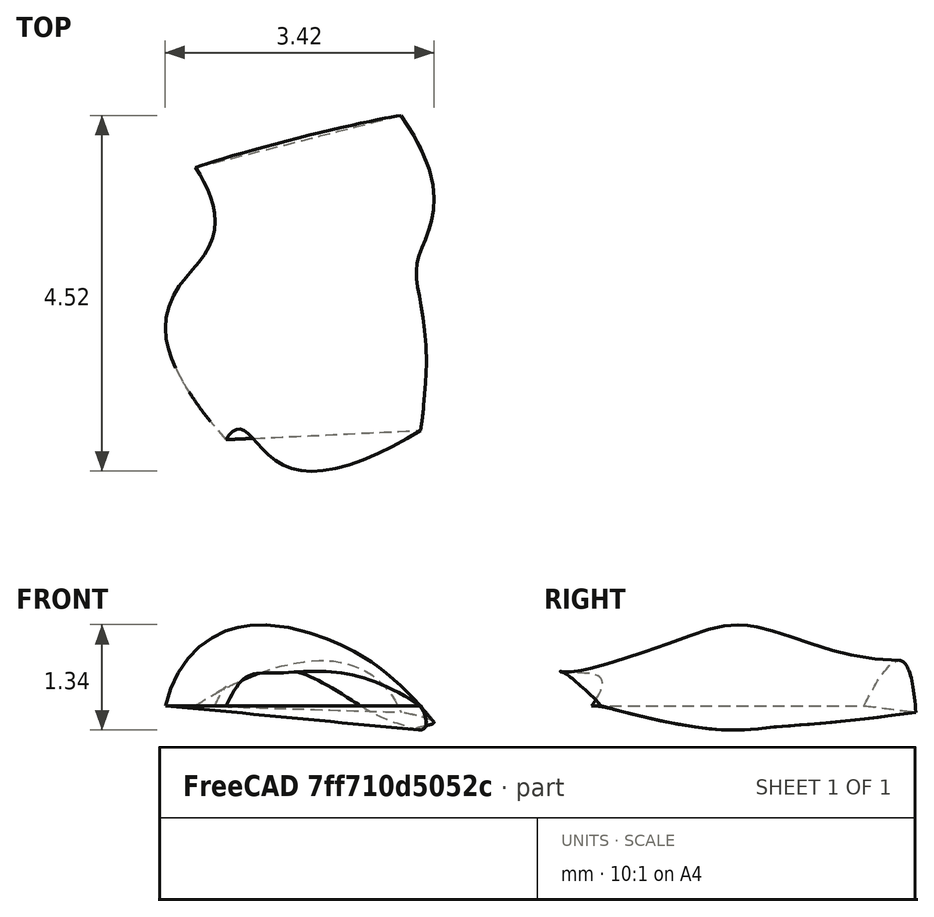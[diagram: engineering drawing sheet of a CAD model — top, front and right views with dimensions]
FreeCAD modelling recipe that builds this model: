
FCSTD DOCUMENT  (FreeCAD 0.17R11203 (Git))
Label: test-birail
License: All rights reserved
LicenseURL: http://en.wikipedia.org/wiki/All_rights_reserved
objects: Part::FeaturePython×5, Part::Spline×2, Sketcher::SketchObject×1, Part::RuledSurface×1
note: 9 computed .brp shape members not serialized (recipe doc carries the construction recipe); baked Part::Feature solids carry a one-line shape summary decoded from their .brp

FEATURE [Part::Spline] BezierCurve
FEATURE [Part::Spline] BezierCurve001
FEATURE [Part::FeaturePython] Spline005  label="Spline001"  # WARN: FeaturePython — macro-defined, semantics opaque (R4)
  CurvePts = (100) [(-2.04029,1.8495,0),(-2.01526,1.8579,0.0164521),(-1.99009,1.86627,0.0327218),(-1.96478,1.87459,0.0488102),(-1.93936,1.88287,0.0647182),+95 more]
  Degree = 3
  KnotPoints = (2) [(-2.04029,1.8495,0),(0.568181,2.50772,-0.0815071)]
  Knots = [0,1]
  Mults = [4,4]
  Pole = 1
  Poles = (4) [(-2.04029,1.8495,0),(-1.28566,2.10427,0.5),(0.0806979,2.43663,1.02805),(0.568181,2.50772,-0.0815071)]
  W = 1
  Weights = [1,1,1,1]
  X = -2.04029
  Y = 1.8495
  Z = 0
FEATURE [Part::FeaturePython] Spline006  label="Spline002"  # WARN: FeaturePython — macro-defined, semantics opaque (R4)
  CurvePts = (100) [(-2.29327,0.272739,0),(-2.28135,0.275926,0.0394779),(-2.26876,0.27916,0.078748),(-2.2555,0.282398,0.117794),(-2.24154,0.285593,0.156598),+95 more]
  Degree = 8
  KnotPoints = (2) [(-2.29327,0.272739,0),(0.767651,0.601303,-0.282289)]
  Knots = [0,1]
  Mults = [9,9]
  Pole = 2
  Poles = (9) [(-2.29327,0.272739,0),(-2,0.352284,1),(-1.46647,0.437994,1.10439),(-1.02507,-0.56493,1.5),(-0.405961,0.646671,0.76721),(0,0.189415,0.396952),+3 more]
  W = 1
  Weights = [1,1,1,1,1,1,1,1,1]
  X = -2
  Y = 0.352284
  Z = 1
FEATURE [Part::FeaturePython] Spline007  label="Spline003"  # WARN: FeaturePython — macro-defined, semantics opaque (R4)
  CurvePts = (100) [(-1.65255,-1.60946,0),(-1.64139,-1.59239,0.0235291),(-1.62987,-1.57584,0.0472614),(-1.61795,-1.5599,0.0712084),(-1.60556,-1.54467,0.0953801),+95 more]
  Degree = 3
  KnotPoints = (3) [(-1.65255,-1.60946,0),(-0.794436,-1.41974,0.297923),(0.815502,-1.49252,0)]
  Knots = [0,1,2]
  Mults = [4,1,4]
  Pole = 3
  Poles = (5) [(-1.65255,-1.60946,0),(-1.41734,-1.239,0.501302),(-1.2,-2.21438,0.3),(-0.0208498,-2.0112,0.561837),(0.815502,-1.49252,0)]
  W = 1
  Weights = [1,1,1,1,1]
  X = -1.2
  Y = -2.21438
  Z = 0.3
FEATURE [Sketcher::SketchObject] Sketch
  sketch-geometry (8):
    g0: LineSegment [constr] StartX=0 StartY=0 StartZ=0 EndX=1 EndY=0 EndZ=0
    g1: LineSegment [constr] StartX=1 StartY=0 StartZ=0 EndX=1 EndY=1 EndZ=0
    g2: LineSegment [constr] StartX=1 StartY=1 StartZ=0 EndX=0 EndY=1 EndZ=0
    g3: LineSegment [constr] StartX=0 StartY=1 StartZ=0 EndX=0 EndY=0 EndZ=0
    g4: ArcOfCircle CenterX=0.31467 CenterY=0.61462 CenterZ=0 NormalX=0 NormalY=0 NormalZ=1 Radius=0.196568 StartAngle=1.5708 EndAngle=4.71239
    g5: ArcOfCircle CenterX=0.718803 CenterY=0.61462 CenterZ=0 NormalX=0 NormalY=0 NormalZ=1 Radius=0.196568 StartAngle=4.71239 EndAngle=7.85398
    g6: LineSegment StartX=0.31467 StartY=0.418051 StartZ=0 EndX=0.718803 EndY=0.418051 EndZ=0
    g7: LineSegment StartX=0.31467 StartY=0.811188 StartZ=0 EndX=0.718803 EndY=0.811188 EndZ=0
  constraints (16):
    c: Coincident(g0,g1)
    c: Coincident(g1,g2)
    c: Coincident(g2,g3)
    c: Coincident(g3,g0)
    c: Horizontal(g0)
    c: Vertical(g1)
    c: Vertical(g3)
    c: Coincident(g0,g-1)
    c: DistanceX(g2,g2) = 1
    c: DistanceY(g1,g1) = 1
    c: Tangent(g4,g7) = 1.5708
    c: Tangent(g4,g6) = -1.5708
    c: Tangent(g6,g5) = -1.5708
    c: Tangent(g7,g5) = 1.5708
    c: Horizontal(g6)
    c: Equal(g4,g5)
FEATURE [Part::RuledSurface] Ruled_Surface
  Curve1 = -> BezierCurve [Edge1]
  Curve2 = -> BezierCurve001 [Edge1]
  Orientation = 0
FEATURE [Part::FeaturePython] Sweep_2_rails  # WARN: FeaturePython — macro-defined, semantics opaque (R4)
  Birail = -> Ruled_Surface
  Blending = 0
  Extend = false
  Parametrization = 0
  ProfileSamples = 20
  Profiles = -> [Spline005,Spline006,Spline007]
  RailSamples = 40
FEATURE [Part::FeaturePython] Approximation_Curve  # WARN: FeaturePython — macro-defined, semantics opaque (R4)
  ApproxTolerance = 0.00581607
  ClampEnds = false
  Continuity = 3
  CurvatureWeight = 1
  DegreeMax = 8
  DegreeMin = 3
  FirstIndex = 0
  LastIndex = 19
  LengthWeight = 1
  Method = 0
  Parametrization = 0
  PointObject = -> Sweep_2_rails
  TorsionWeight = 1
